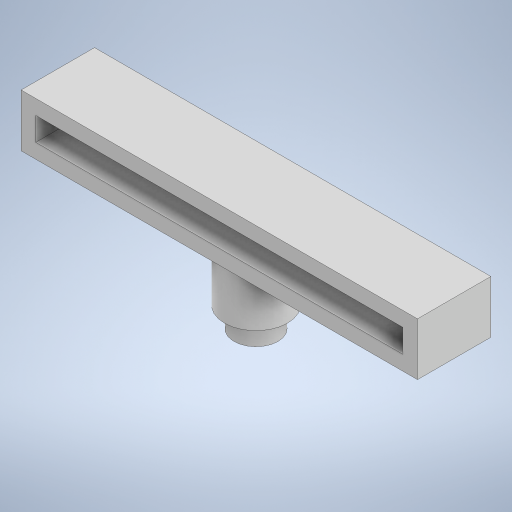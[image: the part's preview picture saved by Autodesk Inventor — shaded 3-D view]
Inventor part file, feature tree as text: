
AUTODESK INVENTOR PART (.ipt)
format: ipt  version: 2023 (Build 270158000, 158)  size: 242,688 bytes
history: native  units: mm
features: extrude x3, sketch x3
ambient origin geometry x8: Origin, YZ Plane, XZ Plane, XY Plane, X Axis, Y Axis, Z Axis, Center Point
bodies: Solid1 (feature_tree)
feature tree (6):
  extrude  "Extrusion1"  Depth=6.35mm
  extrude  "Extrusion2"  Depth=20.0mm TaperAngle=0.0deg
  extrude  "Extrusion3"  Depth=20.0mm TaperAngle=0.0deg
  sketch  "Sketch1"  dims[d0=100.0mm d1=6.35mm]
  sketch  "Sketch2"  dims[d2=4.0mm d3=20.0mm d4=0.0mm]
  sketch  "Sketch3"  dims[d5=12.0mm d6=20.0mm d7=0.0mm d8=17.145mm d9=14.4mm d10=0.0mm]
